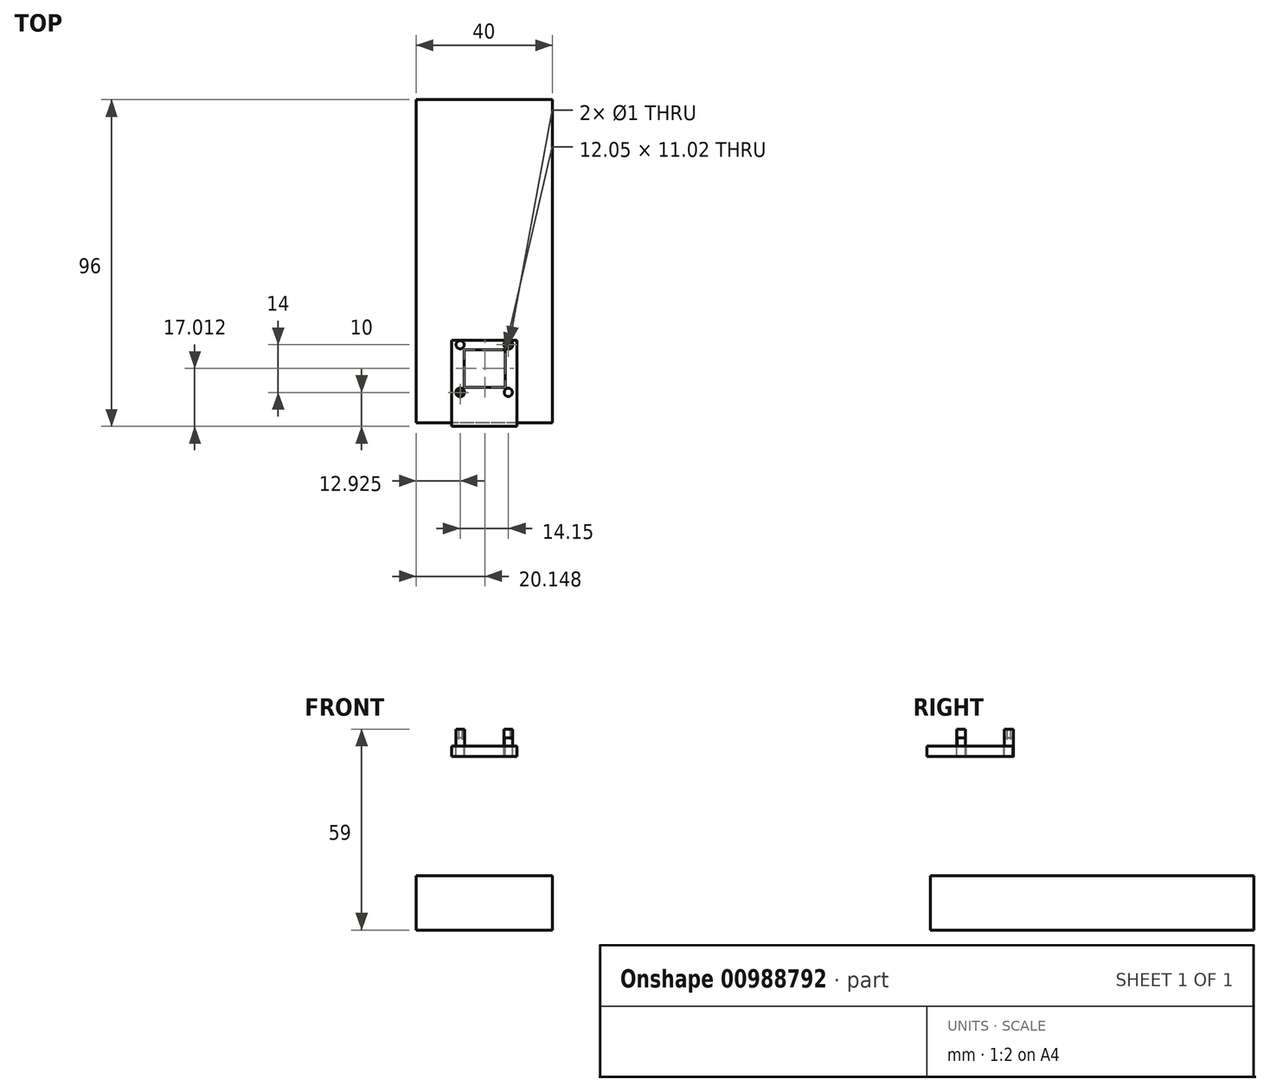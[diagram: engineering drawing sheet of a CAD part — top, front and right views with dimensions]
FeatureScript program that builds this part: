
annotation { "Feature Type Name" : "Feature", "Feature Type Description" : "" }
export const myFeature = defineFeature(function(context is Context, id is Id, definition is map)
    precondition{}
    {
        {
            var Q0;
            Q0=qCreatedBy(makeId("Top.planeOp"),FACE);
            var sketch = newSketch(context, id + "F0", { "sketchPlane" : qUnion([Q0])});
            skCircle(sketch, "E0", {"center": v(7.08, 7) * mm, "radius": 1.3 * mm});
            skLineSegment(sketch, "E1", {"start": v(7.08, 7) * mm, "end": v(-7.08, 7) * mm, "construction": true});
            skCircle(sketch, "E2", {"center": v(-7.07, -7) * mm, "radius": 1.3 * mm});
            skLineSegment(sketch, "E3", {"start": v(7.08, 7) * mm, "end": v(7.08, -7) * mm, "construction": true});
            skLineSegment(sketch, "E4", {"start": v(-7.08, 7) * mm, "end": v(-7.08, -7) * mm, "construction": true});
            skLineSegment(sketch, "E5", {"start": v(-7.07, -7) * mm, "end": v(7.08, -7) * mm, "construction": true});
            skSolve(sketch);
        }
        {
            var Q0;
            Q0=qSketchRegion(id+"F0",true);
            extrude(context, id + "F1", {"entities" : qUnion([Q0]), "depth" : 5 * mm, "offsetDistance" : 25 * mm});
        }
        {
            var Q0;
            Q0=qCreatedBy(makeId("Top.planeOp"),FACE);
            var sketch = newSketch(context, id + "F2", { "sketchPlane" : qUnion([Q0])});
            skCircle(sketch, "E6", {"center": v(-7.08, -7) * mm, "radius": 0.5 * mm});
            skCircle(sketch, "E7", {"center": v(7.08, 7) * mm, "radius": 0.5 * mm});
            skSolve(sketch);
        }
        {
            var Q0;
            Q0=qSketchRegion(id+"F2",true);
            extrude(context, id + "F3", {"entities" : qUnion([Q0]), "operationType" : NewBodyOperationType.REMOVE, "depth" : 5 * mm, "offsetDistance" : 25 * mm});
        }
        {
            var Q0;
            Q0=qCreatedBy(makeId("Top.planeOp"),FACE);
            var sketch = newSketch(context, id + "F4", { "sketchPlane" : qUnion([Q0])});
            skLineSegment(sketch, "E8", {"start": v(-9.57, -17) * mm, "end": v(-9.58, 8.25) * mm});
            skLineSegment(sketch, "E9", {"start": v(-9.58, 8.25) * mm, "end": v(9.57, 8.25) * mm});
            skLineSegment(sketch, "E10", {"start": v(9.58, -17) * mm, "end": v(-9.57, -17) * mm});
            skLineSegment(sketch, "E11", {"start": v(9.58, -17) * mm, "end": v(9.57, 8.25) * mm});
            skLineSegment(sketch, "E12.bottom", {"start": v(-5.88, -5.5) * mm, "end": v(6.17, -5.5) * mm});
            skLineSegment(sketch, "E12.top", {"start": v(-5.88, 5.52) * mm, "end": v(6.17, 5.52) * mm});
            skLineSegment(sketch, "E12.left", {"start": v(-5.88, -5.5) * mm, "end": v(-5.88, 5.52) * mm});
            skLineSegment(sketch, "E12.right", {"start": v(6.17, -5.5) * mm, "end": v(6.17, 5.52) * mm});
            skSolve(sketch);
        }
        {
            var Q0;
            Q0=qSketchRegion(id+"F4",true);
            extrude(context, id + "F5", {"entities" : qUnion([Q0]), "oppositeDirection" : true, "depth" : 3 * mm, "offsetDistance" : 25 * mm});
        }
        {
            var Q0;
            Q0=qSketchRegion(id+"F0",true);
            extrude(context, id + "F6", {"entities" : qUnion([Q0]), "oppositeDirection" : true, "depth" : 3 * mm, "offsetDistance" : 25 * mm});
        }
        {
            var Q0;
            Q0=qCreatedBy(makeId("Top.planeOp"),FACE);
            var sketch = newSketch(context, id + "F7", { "sketchPlane" : qUnion([Q0])});
            skCircle(sketch, "E13", {"center": v(-7.08, 7) * mm, "radius": 1.2 * mm});
            skCircle(sketch, "E14", {"center": v(7.08, -7) * mm, "radius": 1.2 * mm});
            skSolve(sketch);
        }
        {
            var Q0;
            Q0=qSketchRegion(id+"F7",true);
            extrude(context, id + "F8", {"entities" : qUnion([Q0]), "operationType" : NewBodyOperationType.ADD, "depth" : 2.5 * mm, "offsetDistance" : 25 * mm});
        }
        {
            var Q0;
            Q0=qCreatedBy(makeId("Right.planeOp"),FACE);
            var sketch = newSketch(context, id + "F9", { "sketchPlane" : qUnion([Q0])});
            skLineSegment(sketch, "E15.bottom", {"start": v(-16, -38) * mm, "end": v(79, -38) * mm});
            skLineSegment(sketch, "E15.top", {"start": v(-16, -54) * mm, "end": v(79, -54) * mm});
            skLineSegment(sketch, "E15.left", {"start": v(-16, -38) * mm, "end": v(-16, -54) * mm});
            skLineSegment(sketch, "E15.right", {"start": v(79, -38) * mm, "end": v(79, -54) * mm});
            skSolve(sketch);
        }
        {
            var Q0;
            Q0 = qSketchRegion(id + "F9", true);
            extrude(context, id + "F10", {"entities" : qUnion([Q0]), "depth" : 20 * mm, "offsetDistance" : 25 * mm, "hasSecondDirection" : true, "secondDirectionOppositeDirection" : true, "secondDirectionDepth" : 20 * mm});
        }
    });
